# Revit family: TSL.R030
name_source: partatom
category: Specialty Equipment
revit_build: Autodesk Revit 2017 (Build: 20160225_1515(x64)
units: mm (PartAtom-declared; Revit-internal decimal feet)

## family parameters
Cut with Voids When Loaded = No
Host = Face
OmniClass Number = 23.40.20.21.14
OmniClass Title = Hand and Hair Dryers
Part Type = Normal
Room Calculation Point = No
Round Connector Dimension = Use Diameter
Shared = No

## types (1)
- TSL.R030
    Assembly Code = E1010900
    AssetType = fixed
    BIMObjectName = TSL.R030
    Default Elevation = 1500 mm
    DocumentationInstallationGuide = https://thesplashlab.com
    DocumentationLiterature = https://thesplashlab.com
    DocumentationMaintenance = https://thesplashlab.com
    DocumentationTechnical = https://thesplashlab.com
    DurationUnit = year
    ExpectedLife = 3
    Finish = Brushed
    Grade = 304
    IfcExportAs = IfcBuildingElementProxy
    IfcExportType = HANDDRYER
    Keynote = N13/360
    Manufacturer = The Splash Lab
    ManufacturerURL = https://thesplashlab.com
    Material = Stainless Steel
    Model = TSL.R030
    ModelNumber = TSL.R030
    NBSReference = 45-35-72/334
    Name = TSL.R030
    NominalHeight = 176 mm
    NominalLength = 233 mm
    NominalWidth = 55 mm
    Product Documentation Link = https://thesplashlab.com
    Product O&M Link = https://thesplashlab.com
    Product Page Link = https://thesplashlab.com
    Product Specification Link = https://thesplashlab.com
    ProductInformation = https://thesplashlab.com
    Type Comments = Mains power, Satin Finish
    TypeName = TSL.R030
    URL = https://thesplashlab.com
    Uniclass2 = 45-35-72/334
    Version = 0
    WarrantyDescription = 2 years from date of purchase
    WarrantyDurationParts = 3
    WarrantyDurationUnit = year
    WarrantyGuarantorParts = https://thesplashlab.com
    material = Steel-Lovair-Satin

## geometry (parser evidence)
native form markers: Sweep x3
no freeform markers — native parametric forms only
